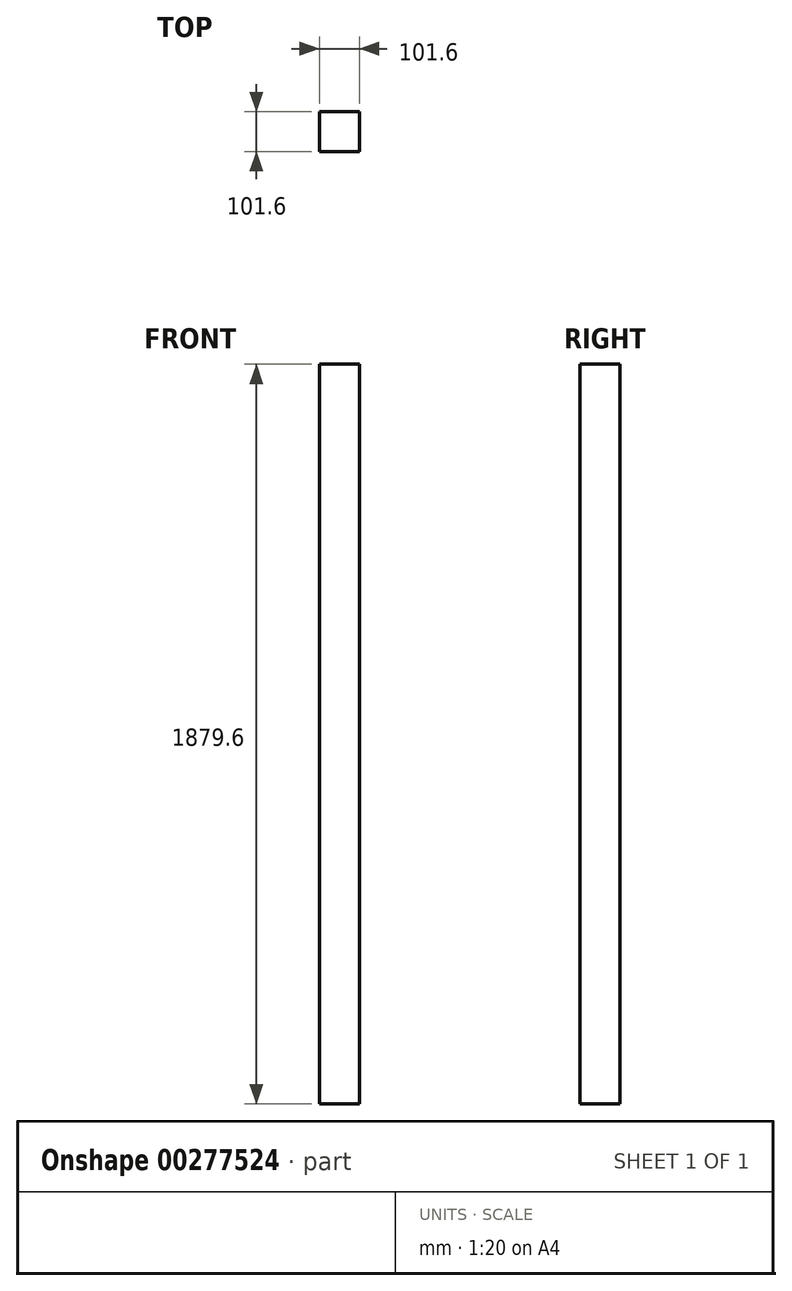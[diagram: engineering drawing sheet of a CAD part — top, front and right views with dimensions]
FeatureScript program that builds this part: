
annotation { "Feature Type Name" : "Feature", "Feature Type Description" : "" }
export const myFeature = defineFeature(function(context is Context, id is Id, definition is map)
    precondition{}
    {
        {
            var Q0;
            Q0=qCreatedBy(makeId("Top.planeOp"),FACE);
            var sketch = newSketch(context, id + "F0", { "sketchPlane" : qUnion([Q0])});
            skLineSegment(sketch, "E0.bottom", {"start": v(-50.8, -50.8) * mm, "end": v(50.8, -50.8) * mm});
            skLineSegment(sketch, "E0.top", {"start": v(-50.8, 50.8) * mm, "end": v(50.8, 50.8) * mm});
            skLineSegment(sketch, "E0.left", {"start": v(-50.8, -50.8) * mm, "end": v(-50.8, 50.8) * mm});
            skLineSegment(sketch, "E0.right", {"start": v(50.8, -50.8) * mm, "end": v(50.8, 50.8) * mm});
            skPoint(sketch, "E0.middle", {"position": v(0, 0) * mm});
            skSolve(sketch);
        }
        {
            var Q0;
            Q0=makeQuery(id+"F0.imprint","IMPRINT",FACE,{"disambiguationData":[TD([[makeQuery(id+"F0.imprint","IMPRINT",EDGE,{"derivedFrom":sQuery(id+"F0.wireOp",EDGE,"E0.bottom")}),1.0]])]});
            extrude(context, id + "F1", {"entities" : qUnion([Q0]), "depth" : 1879.6 * mm});
        }
    });
